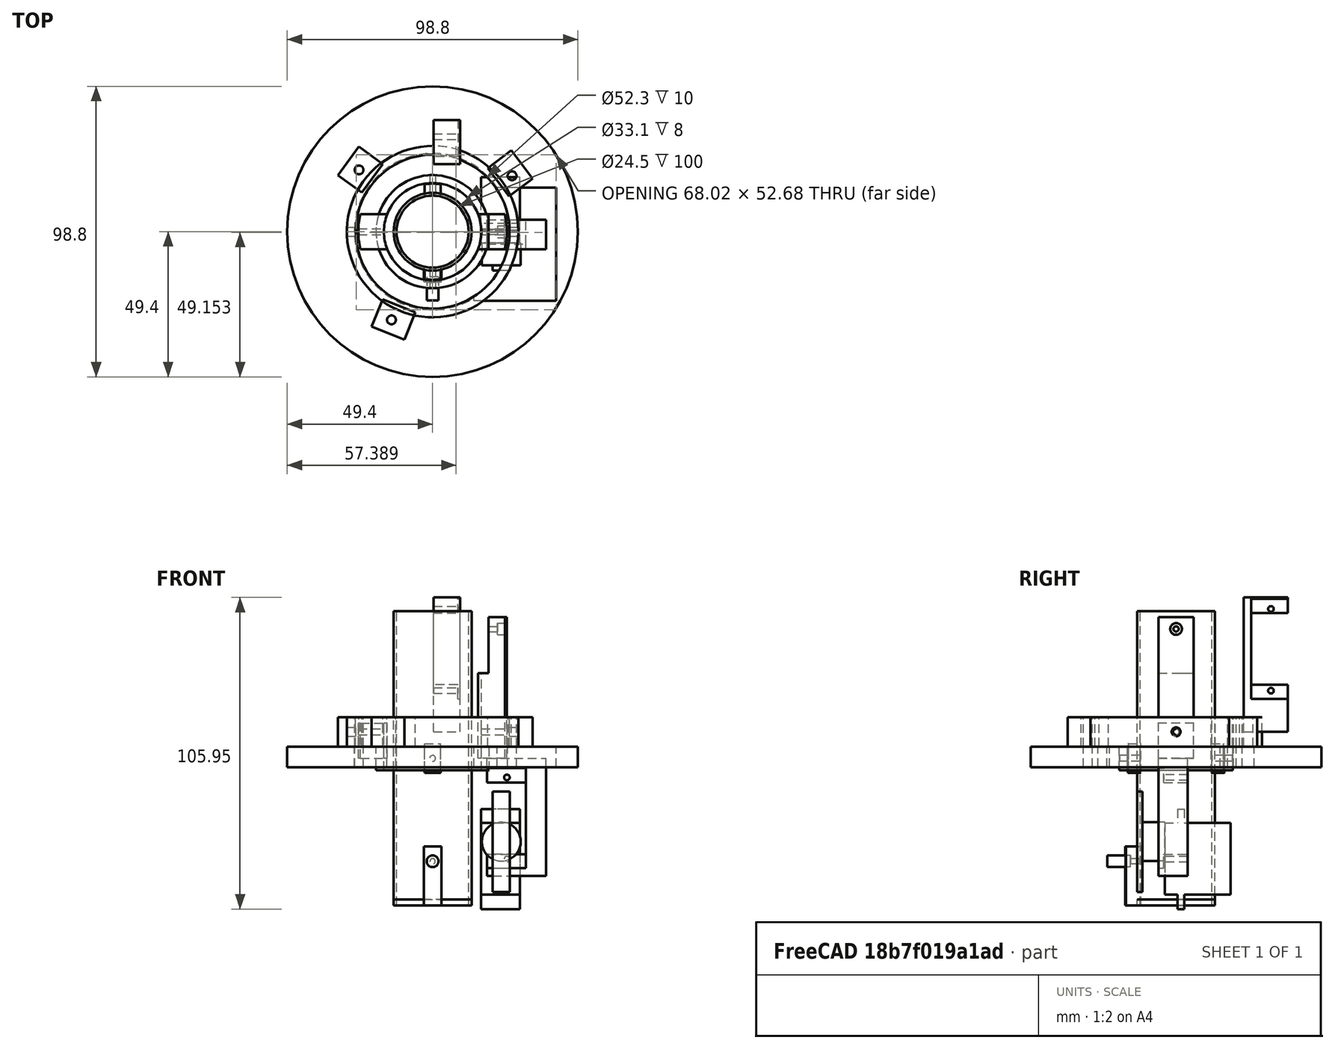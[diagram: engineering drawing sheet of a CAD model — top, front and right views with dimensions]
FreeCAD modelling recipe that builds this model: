
FCSTD DOCUMENT  (FreeCAD 0.18R16146 (Git))
Label: Gimbal
License: All rights reserved
LicenseURL: http://en.wikipedia.org/wiki/All_rights_reserved
objects: Part::Cylinder×28, Part::Cut×24, Part::Box×18, Part::MultiFuse×16, Spreadsheet::Sheet×1
note: 86 computed .brp shape members not serialized (recipe doc carries the construction recipe); baked Part::Feature solids carry a one-line shape summary decoded from their .brp

FEATURE [Part::Cylinder] Cylinder  label="Estes24mm"
  Angle = 360
  AttacherType = Attacher::AttachEngine3D
  Height = 100
  Radius = 12.25
  expr: Height = Spreadsheet.Estes24mmLength
  expr: Radius = Spreadsheet.Estes24mmRadius
FEATURE [Part::Cylinder] Cylinder001  label="EngineHolder"
  Angle = 360
  AttacherType = Attacher::AttachEngine3D
  Height = 100
  Radius = 13.25
  expr: Radius = Spreadsheet.EngineHolderOuterRadius
  expr: Height = Spreadsheet.EngineHolderLength
FEATURE [Spreadsheet::Sheet] Spreadsheet
  cells = A1=EngineHolderLength; B1(EngineHolderLength)=100; A2=EngineHolderOuterRadius; B2(EngineHolderOuterRadius)=13.25; A3=WidthServo; B3(WidthServo)=13.2; A4=xScrewMountThickness; B4(xScrewMountThickness)=3; A5=ScrewMountZ; B5(ScrewMountZ)=10; A6=ScrewMountX; B6(ScrewMountX)=5.5; C6=For width of ScrewBoss On Motor Mount Tube; A7=Bracket1Thickness; B7(BracketThickness1)=3; A8=Bracket1Height; B8(Bracket1Height)=8; A9=Bracket1InnerTolerance; B9(Bracket1InnerTolerance)=0.3; A10=PushpointFromBottom1; B10(PushpointFromBottom1)=0; C10=Bottom of PushPointProtrusion (what holds the linkage stopper); A11=PushpointHeight1; B11(PushpointHeight1)=4; A12=PushpointLenght1; B12(PushpointLength1)=20; A13=PushpointWidth1; B13(PushpointWidth1)=6; A14=Estes24mmRadius; B14(Estes24mmRadius)=12.25; A15=ServoScrewSeparation; B15(ServoScrewSeparation)=27.8; A16=ScrewMountWidthY; B16(ScrewMountWidthY)=12; C16=For Width of ScrewBoss on Bracket1; A17=Bracket2InnerTolerance; B17(Bracket2InnerTolerance)=0.9; C17=radial distance or wiggle room between bracket 1 and 2; A18=Bracket2Thickness; B18(Bracket2Thickness)=3; C18=thickness of outer bracket (bracket 2); A19=ScrewBracket1Thickness; B19(ScrewBracket1Thickkness)=9; C19=thickness of screw bosses to attach bracket 1 and 2; A20=Estes24mmLength; B20(Estes24mmLength)=100; C20=Length of Engine; actually making it longer to completely hollow cylinder; A21=Bracket1Center; B21(Bracket1Center)=50; C21=Distance from Bottom of EngineHolder to First Bracket (z); A22=YScrewHoleZ; B22(YScrewHoleZ)=5; C22=Distance from Bottom of Y ScrewBoss to ScrewCenter; A23=Bracket1LongZ; B23(Bracket1LongZ)=48; C23=Length of Long Part of Bracket1 Arm; A24=ScrewPointOuterGimbal; B24(ScrewPointOuterGimbal)==Spreadsheet.Bracket1Center + Spreadsheet.Bracket1Height / 2 + Spreadsheet.YScrewHoleZ; C24=Distance from Bottom of Mount to Where Outer Gimbal Screws; A25=DisRotPushPoint; B25(DisRotPushPoint)=35; C25=Distance from Screws to Where Servo Pushes (in Z); A26=LinkageStopperZ; B26(LinkageStopperZ)=15; C26=Distance to LinkageStopperScrewIn from Bottom in Z
FEATURE [Part::Cut] Cut  label="A-EngineHolderSubtractedEngine"
  Base = -> Cylinder001
  Tool = -> Cylinder
FEATURE [Part::Box] Box  label="Cube"
  AttacherType = Attacher::AttachEngine3D
  Height = 24.4
  Length = 13.2
  Width = 22.4
  expr: Length = Spreadsheet.WidthServo
FEATURE [Part::Box] Box001  label="Cube001"
  AttacherType = Attacher::AttachEngine3D
  Height = 34
  Length = 13.2
  Placement = pos=(0,4.3,-4.75) rot=(0,0,1;0rad)
  Width = 2.3
  expr: Length = Spreadsheet.WidthServo
FEATURE [Part::Cylinder] Cylinder002  label="Cylinder"
  Angle = 360
  AttacherType = Attacher::AttachEngine3D
  Height = 7.6
  Placement = pos=(6.35,0,6.35) rot=(1,0,0;1.5708rad)
  Radius = 6.6
  expr: Radius = Spreadsheet.WidthServo / 2
FEATURE [Part::Box] Box002  label="Rotor"
  AttacherType = Attacher::AttachEngine3D
  Height = 34.2
  Length = 5.8
  Placement = pos=(3.45,-9.4,-10.75) rot=(0,0,1;0rad)
  Width = 1.8
FEATURE [Part::MultiFuse] Fusion  label="Servo"
  Placement = pos=(29.7,-3.85,28) rot=(0,1,0;3.14159rad)
  Shapes = -> [Box,Cylinder002,Box002,Box001]
  expr: Placement.Base.y = 9.4 - Spreadsheet.EngineHolderOuterRadius
FEATURE [Part::Cylinder] Cylinder004  label="MountBracket1"
  Angle = 360
  AttacherType = Attacher::AttachEngine3D
  Height = 10
  Placement = pos=(0,0,45) rot=(0,0,1;0rad)
  Radius = 16.35
  expr: Placement.Base.z = Spreadsheet.EngineHolderLength / 2 - Spreadsheet.ScrewMountZ / 2
  expr: Radius = Spreadsheet.EngineHolderOuterRadius + Spreadsheet.xScrewMountThickness + Spreadsheet.Bracket1InnerTolerance / 3
  expr: Height = Spreadsheet.ScrewMountZ
FEATURE [Part::Cylinder] Cylinder005  label="Estes24mm001"
  Angle = 360
  AttacherType = Attacher::AttachEngine3D
  Height = 94.5
  Radius = 12.25
  expr: Radius = Spreadsheet.Estes24mmRadius
FEATURE [Part::Cut] Cut001  label="MountBracket"
  Base = -> Cylinder004
  Tool = -> Cylinder005
FEATURE [Part::Box] Box003  label="Cube002"
  AttacherType = Attacher::AttachEngine3D
  Height = 100
  Length = 16.25
  Placement = pos=(2.75,-16.25,0) rot=(0,0,1;0rad)
  Width = 32.5
  expr: Placement.Base.y = -Spreadsheet.EngineHolderOuterRadius - Spreadsheet.xScrewMountThickness
  expr: Width = Spreadsheet.EngineHolderOuterRadius * 2 + Spreadsheet.xScrewMountThickness * 2
  expr: Length = Spreadsheet.EngineHolderOuterRadius + Spreadsheet.xScrewMountThickness
  expr: Height = Spreadsheet.EngineHolderLength
  expr: Placement.Base.x = Spreadsheet.ScrewMountX / 2
FEATURE [Part::Box] Box004  label="Cube003"
  AttacherType = Attacher::AttachEngine3D
  Height = 100
  Length = 16
  Placement = pos=(-18.75,-16.25,0) rot=(0,0,1;0rad)
  Width = 32.5
  expr: Placement.Base.y = -Spreadsheet.EngineHolderOuterRadius - Spreadsheet.xScrewMountThickness
  expr: Width = Spreadsheet.EngineHolderOuterRadius * 2 + Spreadsheet.xScrewMountThickness * 2
  expr: Length = Spreadsheet.EngineHolderOuterRadius + Spreadsheet.ScrewMountX / 2
  expr: Height = Spreadsheet.EngineHolderLength
  expr: Placement.Base.x = -Spreadsheet.ScrewMountX - Spreadsheet.EngineHolderOuterRadius
FEATURE [Part::MultiFuse] Fusion001  label="SubtractionCubesForMountBracket"
  Shapes = -> [Box003,Box004]
FEATURE [Part::Cut] Cut002  label="MountBracketForScrews"
  Base = -> Cut001
  Tool = -> Fusion001
FEATURE [Part::Cylinder] Cylinder006  label="OuterCylinderBracket1"
  Angle = 360
  AttacherType = Attacher::AttachEngine3D
  Height = 8
  Radius = 19.25
  expr: Radius = Spreadsheet.EngineHolderOuterRadius + Spreadsheet.xScrewMountThickness + Spreadsheet.BracketThickness1
  expr: Height = Spreadsheet.Bracket1Height
FEATURE [Part::Cylinder] Cylinder007  label="InnerCylinderBracket"
  Angle = 360
  AttacherType = Attacher::AttachEngine3D
  Height = 8
  Radius = 16.55
  expr: Radius = Spreadsheet.EngineHolderOuterRadius + Spreadsheet.xScrewMountThickness + Spreadsheet.Bracket1InnerTolerance
  expr: Height = Spreadsheet.Bracket1Height
FEATURE [Part::Cut] Cut003  label="Bracket1"
  Base = -> Cylinder006
  Placement = pos=(0,0,46) rot=(0,0,1;0rad)
  Tool = -> Cylinder007
  expr: Placement.Base.z = Spreadsheet.Bracket1Center - Spreadsheet.Bracket1Height / 2
FEATURE [Part::Cylinder] Cylinder008  label="PushPoint1"
  Angle = 360
  AttacherType = Attacher::AttachEngine3D
  Height = 20
  Radius = 17.25
  expr: Height = Spreadsheet.PushpointLength1
  expr: Radius = Spreadsheet.EngineHolderOuterRadius + Spreadsheet.PushpointHeight1
  expr: Placement.Base.z = Spreadsheet.PushpointFromBottom1
FEATURE [Part::Cylinder] Cylinder009  label="Estes24mm002"
  Angle = 360
  AttacherType = Attacher::AttachEngine3D
  Height = 94.5
  Radius = 12.25
  expr: Radius = Spreadsheet.Estes24mmRadius
FEATURE [Part::Cut] Cut004  label="PushpointOne"
  Base = -> Cylinder008
  Tool = -> Cylinder009
FEATURE [Part::Box] Box005  label="Cube004"
  AttacherType = Attacher::AttachEngine3D
  Height = 80
  Length = 50
  Placement = pos=(3,-30,-5) rot=(0,0,1;0rad)
  Width = 100
  expr: Placement.Base.x = Spreadsheet.PushpointWidth1 / 2
FEATURE [Part::Box] Box006  label="Cube005"
  AttacherType = Attacher::AttachEngine3D
  Height = 80
  Length = 60
  Placement = pos=(-63,-30,-5) rot=(0,0,1;0rad)
  Width = 100
  expr: Placement.Base.x = -60 - Spreadsheet.PushpointWidth1 / 2
FEATURE [Part::Box] Box007  label="Cube006"
  AttacherType = Attacher::AttachEngine3D
  Height = 80
  Length = 40
  Placement = pos=(-20,0,-5) rot=(0,0,1;0rad)
  Width = 30
FEATURE [Part::MultiFuse] Fusion002  label="SubtractionCubes"
  Shapes = -> [Box005,Box006,Box007]
FEATURE [Part::Cut] Cut005  label="PushPointFirst"
  Base = -> Cut004
  Tool = -> Fusion002
FEATURE [Part::Cylinder] Cylinder010  label="BigHead"
  Angle = 360
  AttacherType = Attacher::AttachEngine3D
  Height = 7.9
  Placement = pos=(0,-3.1,0) rot=(1,0,0;1.5708rad)
  Radius = 2
FEATURE [Part::Cylinder] Cylinder011  label="SmallScrewCylinder"
  Angle = 360
  AttacherType = Attacher::AttachEngine3D
  Height = 3.1
  Placement = pos=(0,0,0) rot=(1,0,0;1.5708rad)
  Radius = 0.9
FEATURE [Part::MultiFuse] Fusion006  label="LinkageStopper"
  Placement = pos=(0,-12.35,15) rot=(0,0,1;0rad)
  Shapes = -> [Cylinder010,Cylinder011]
  expr: Placement.Base.z = Spreadsheet.LinkageStopperZ
  expr: Placement.Base.y = -(Spreadsheet.EngineHolderOuterRadius + Spreadsheet.PushpointHeight1) + 4.9
  expr: Placement.Base.x = 0
FEATURE [Part::MultiFuse] Fusion007  label="LinkageStopper001"
  Placement = pos=(0,-12.35,15) rot=(0,0,1;0rad)
  Shapes = -> [Cylinder010,Cylinder011]
  expr: Placement.Base.z = Spreadsheet.LinkageStopperZ
  expr: Placement.Base.y = -(Spreadsheet.EngineHolderOuterRadius + Spreadsheet.PushpointHeight1) + 4.9
  expr: Placement.Base.x = 0
FEATURE [Part::Cut] Cut008  label="A-PushPointWithHole"
  Base = -> Cut005
  Tool = -> Fusion007
FEATURE [Part::Cylinder] Cylinder012  label="ScrewSubtractionCylinderForFirstMount"
  Angle = 360
  AttacherType = Attacher::AttachEngine3D
  Height = 90
  Placement = pos=(0,45,50) rot=(1,0,0;1.5708rad)
  Radius = 1
  expr: Placement.Base.z = Spreadsheet.EngineHolderLength / 2
FEATURE [Part::Cut] Cut009  label="A-MountBracketForScrewsWithScrewHole"
  Base = -> Cut002
  Tool = -> Cylinder012
FEATURE [Part::Cylinder] Cylinder013  label="ScrewSubtractionCylinderForFirstMount001"
  Angle = 360
  AttacherType = Attacher::AttachEngine3D
  Height = 90
  Placement = pos=(0,45,50) rot=(1,0,0;1.5708rad)
  Radius = 1
  expr: Placement.Base.z = Spreadsheet.Bracket1Center
FEATURE [Part::Cut] Cut010  label="B-Bracket1WithScrewHole"
  Base = -> Cut003
  Tool = -> Cylinder013
FEATURE [Part::Box] Box012  label="HolderCube001"
  AttacherType = Attacher::AttachEngine3D
  Height = 40
  Length = 20
  Placement = pos=(18.5,-6,10) rot=(0,0,1;0rad)
  Width = 10
FEATURE [Part::MultiFuse] Fusion008  label="Servo001"
  Placement = pos=(18.5,-10.75,17.4) rot=(0,0,1;0rad)
  Shapes = -> [Box,Cylinder002,Box002,Box001]
FEATURE [Part::Cut] Cut011  label="ServoHolder001"
  Base = -> Box012
  Tool = -> Fusion008
FEATURE [Part::Cylinder] Cylinder014  label="ScrewSubtractionCylinderForServo1"
  Angle = 360
  AttacherType = Attacher::AttachEngine3D
  Height = 90
  Placement = pos=(23.25,47,13.5) rot=(1,0,0;1.5708rad)
  Radius = 0.95
FEATURE [Part::Cylinder] Cylinder015  label="ScrewSubtractionCylinderForServo002"
  Angle = 360
  AttacherType = Attacher::AttachEngine3D
  Height = 90
  Placement = pos=(23.25,47,41.3) rot=(1,0,0;1.5708rad)
  Radius = 0.95
  expr: Placement.Base.z = 13.5 + Spreadsheet.ServoScrewSeparation
FEATURE [Part::MultiFuse] Fusion009  label="ServoScrewRemovalCylinders"
  Placement = pos=(2,0,2.2) rot=(0,0,1;0rad)
  Shapes = -> [Cylinder015,Cylinder014]
FEATURE [Part::Cut] Cut012  label="B-ServoHolderWithScrewsRemoved"
  Base = -> Cut011
  Tool = -> Fusion009
FEATURE [Part::Cylinder] Cylinder016  label="OuterCylinderBracket002"
  Angle = 360
  AttacherType = Attacher::AttachEngine3D
  Height = 48
  Radius = 25.25
  expr: Radius = Spreadsheet.EngineHolderOuterRadius + Spreadsheet.xScrewMountThickness + Spreadsheet.ScrewBracket1Thickkness
  expr: Height = Spreadsheet.Bracket1LongZ
FEATURE [Part::Cylinder] Cylinder017  label="InnerCylinderBracket001"
  Angle = 360
  AttacherType = Attacher::AttachEngine3D
  Height = 48
  Radius = 16.55
  expr: Radius = Spreadsheet.EngineHolderOuterRadius + Spreadsheet.xScrewMountThickness + Spreadsheet.Bracket1InnerTolerance
  expr: Height = Spreadsheet.Bracket1LongZ
FEATURE [Part::Cut] Cut013  label="Bracket1toBracket2"
  Base = -> Cylinder016
  Placement = pos=(0,0,50) rot=(0,0,1;0rad)
  Tool = -> Cylinder017
  expr: Placement.Base.z = Spreadsheet.EngineHolderLength / 2 + 0 * Spreadsheet.Bracket1Height / 2
FEATURE [Part::Cylinder] Cylinder018  label="ScrewSubtractionCylinderForSecondMount"
  Angle = 360
  AttacherType = Attacher::AttachEngine3D
  Height = 90
  Placement = pos=(-45,0,59) rot=(0,1,0;1.5708rad)
  Radius = 1
  expr: Placement.Base.z = Spreadsheet.Bracket1Center + Spreadsheet.Bracket1Height / 2 + Spreadsheet.YScrewHoleZ
FEATURE [Part::Cut] Cut014  label="Bracket1toBracket2Connection"
  Base = -> Cut013
  Tool = -> Cylinder018
FEATURE [Part::Box] Box013  label="Cube007"
  AttacherType = Attacher::AttachEngine3D
  Height = 150
  Length = 100
  Placement = pos=(-50,6,0) rot=(0,0,1;0rad)
  Width = 100
  expr: Placement.Base.y = Spreadsheet.ScrewMountWidthY / 2
FEATURE [Part::Box] Box014  label="Cube008"
  AttacherType = Attacher::AttachEngine3D
  Height = 150
  Length = 100
  Placement = pos=(-50,-6,0) rot=(0,0,-1;1.5708rad)
  Width = 100
  expr: Placement.Base.y = -Spreadsheet.ScrewMountWidthY / 2
FEATURE [Part::MultiFuse] Fusion010  label="SubtractionCubesForYBracket"
  Shapes = -> [Box013,Box014]
FEATURE [Part::Cut] Cut015  label="InnerYScrewBoss"
  Base = -> Cut014
  Tool = -> Fusion010
FEATURE [Part::Cylinder] Cylinder019  label="Bracket1Outer"
  Angle = 360
  AttacherType = Attacher::AttachEngine3D
  Height = 10
  Radius = 29.15
  expr: Radius = Spreadsheet.EngineHolderOuterRadius + Spreadsheet.xScrewMountThickness + Spreadsheet.BracketThickness1 + Spreadsheet.Bracket2InnerTolerance + Spreadsheet.ScrewBracket1Thickkness
FEATURE [Part::Cylinder] Cylinder020  label="Bracket1Inner"
  Angle = 360
  AttacherType = Attacher::AttachEngine3D
  Height = 10
  Radius = 26.15
  expr: Radius = Spreadsheet.EngineHolderOuterRadius + Spreadsheet.xScrewMountThickness + Spreadsheet.ScrewBracket1Thickkness + Spreadsheet.Bracket2InnerTolerance
FEATURE [Part::Cut] Cut016  label="Bracket2Solid"
  Base = -> Cylinder019
  Placement = pos=(0,0,54) rot=(0,0,1;0rad)
  Tool = -> Cylinder020
  expr: Placement.Base.z = Spreadsheet.EngineHolderLength / 2 + Spreadsheet.Bracket1Height / 2
FEATURE [Part::Cylinder] Cylinder021  label="ScrewSubtractionCylinderForSecondMount001"
  Angle = 360
  AttacherType = Attacher::AttachEngine3D
  Height = 90
  Placement = pos=(-45,0,59) rot=(0,1,0;1.5708rad)
  Radius = 1.5
  expr: Placement.Base.z = Spreadsheet.Bracket1Center + Spreadsheet.Bracket1Height / 2 + Spreadsheet.YScrewHoleZ
FEATURE [Part::Cut] Cut017  label="C-Bracket2WithScrewHoles"
  Base = -> Cut016
  Tool = -> Cylinder021
FEATURE [Part::Box] Box015  label="SubtractionCubeBackLongBracket"
  AttacherType = Attacher::AttachEngine3D
  Height = 100
  Length = 50
  Placement = pos=(-50,-50,62) rot=(0,0,1;0rad)
  Width = 100
  expr: Placement.Base.z = Spreadsheet.EngineHolderLength / 2 + Spreadsheet.Bracket1Height + Spreadsheet.Bracket1Height / 2
FEATURE [Part::Cut] Cut018  label="YScrewBossPlus2ndPushLength"
  Base = -> Cut015
  Tool = -> Box015
FEATURE [Part::Cylinder] Cylinder022  label="PushPointOuterGimbal"
  Angle = 360
  AttacherType = Attacher::AttachEngine3D
  Height = 90
  Placement = pos=(-45,0,94) rot=(0,1,0;1.5708rad)
  Radius = 0.1
  expr: Placement.Base.z = Spreadsheet.DisRotPushPoint + Spreadsheet.ScrewPointOuterGimbal
FEATURE [Part::MultiFuse] Fusion012  label="ServoScrewRemovalCylinders001"
  Placement = pos=(0,0,0.5) rot=(0,0,1;0rad)
  Shapes = -> [Cylinder015,Cylinder014]
FEATURE [Part::MultiFuse] Fusion013  label="Servo002"
  Placement = pos=(16.5,-3.85,16) rot=(0,0,1;0rad)
  Shapes = -> [Box,Cylinder002,Box002,Box001]
  expr: Placement.Base.y = 9.4 - Spreadsheet.EngineHolderOuterRadius
FEATURE [Part::MultiFuse] Fusion014  label="Servo2wSubtractionHoles"
  Placement = pos=(11.3,9,59) rot=(0,0,1;1.5708rad)
  Shapes = -> [Fusion013,Fusion012]
FEATURE [Part::Cut] Cut019  label="YScrewBossPlusPushArm"
  Base = -> Cut018
  Tool = -> Cylinder022
FEATURE [Part::Box] Box016  label="Servo2Block"
  AttacherType = Attacher::AttachEngine3D
  Height = 45.7
  Length = 9
  Placement = pos=(0.3,23,59) rot=(0,0,1;0rad)
  Width = 15
FEATURE [Part::Cut] Cut020  label="C-Servo2Holder"
  Base = -> Box016
  Tool = -> Fusion014
FEATURE [Part::Box] Box017  label="SubtractionBlockPushArm"
  AttacherType = Attacher::AttachEngine3D
  Height = 21
  Length = 10
  Placement = pos=(9,-8,79) rot=(0,0,1;0rad)
  Width = 16
FEATURE [Part::Cut] Cut021  label="YScrewBossesPlusPushArm"
  Base = -> Cut019
  Tool = -> Box017
FEATURE [Part::MultiFuse] Fusion015  label="LinkageStopper002"
  Placement = pos=(19,0,94) rot=(0,0,1;1.5708rad)
  Shapes = -> [Cylinder010,Cylinder011]
  expr: Placement.Base.z = Spreadsheet.DisRotPushPoint + Spreadsheet.ScrewPointOuterGimbal
  expr: Placement.Base.y = 0
FEATURE [Part::Cut] Cut022  label="B-YScrewBossPlusPushArmSubtractLinkageStopper"
  Base = -> Cut021
  Tool = -> Fusion015
FEATURE [Part::Cylinder] Cylinder023  label="FourInchOuterTube"
  Angle = 360
  AttacherType = Attacher::AttachEngine3D
  Height = 7
  Radius = 49.4
FEATURE [Part::Cylinder] Cylinder024  label="FourInchInner"
  Angle = 360
  AttacherType = Attacher::AttachEngine3D
  Height = 7
  Radius = 26.6
FEATURE [Part::Cut] Cut023  label="FourInchTube"
  Base = -> Cylinder023
  Placement = pos=(0,0,47) rot=(0,0,1;0rad)
  Tool = -> Cylinder024
FEATURE [Part::Box] Box018  label="ScrewBoxBlock1"
  AttacherType = Attacher::AttachEngine3D
  Height = 10
  Length = 10
  Placement = pos=(26,12,54) rot=(0,0,1;0.645772rad)
  Width = 12
  expr: Placement.Base.z = Spreadsheet.EngineHolderLength / 2 + Spreadsheet.Bracket1Height / 2
FEATURE [Part::Box] Box019  label="ScrewBoxBlock002"
  AttacherType = Attacher::AttachEngine3D
  Height = 10
  Length = 10
  Placement = pos=(-17,23,54) rot=(0,0,1;2.51327rad)
  Width = 12
  expr: Placement.Base.z = Spreadsheet.EngineHolderLength / 2 + Spreadsheet.Bracket1Height / 2
FEATURE [Part::Box] Box020  label="ScrewBoxBlock003"
  AttacherType = Attacher::AttachEngine3D
  Height = 10
  Length = 10
  Placement = pos=(-17,-23,54) rot=(0,0,-1;1.95477rad)
  Width = 12
  expr: Placement.Base.z = Spreadsheet.EngineHolderLength / 2 + Spreadsheet.Bracket1Height / 2
FEATURE [Part::Cylinder] Cylinder025  label="MountScrew1"
  Angle = 360
  AttacherType = Attacher::AttachEngine3D
  Height = 100
  Placement = pos=(27,19,0) rot=(0,0,1;0rad)
  Radius = 1.5
FEATURE [Part::Cylinder] Cylinder026  label="MountScrew002"
  Angle = 360
  AttacherType = Attacher::AttachEngine3D
  Height = 100
  Placement = pos=(-25,21,0) rot=(0,0,1;0rad)
  Radius = 1.5
FEATURE [Part::Cylinder] Cylinder027  label="MountScrew003"
  Angle = 360
  AttacherType = Attacher::AttachEngine3D
  Height = 100
  Placement = pos=(-14,-30,0) rot=(0,0,1;0rad)
  Radius = 1.5
FEATURE [Part::MultiFuse] Fusion016  label="MountScrews"
  Shapes = -> [Cylinder025,Cylinder027,Cylinder026]
FEATURE [Part::MultiFuse] Fusion017  label="MountBlocks"
  Shapes = -> [Box018,Box019,Box020]
FEATURE [Part::Cut] Cut024  label="C-MountBlocksWithScrewHoles"
  Base = -> Fusion017
  Tool = -> Fusion016
FEATURE [Part::Box] Box021  label="ServoCutoutWMargin"
  AttacherType = Attacher::AttachEngine3D
  Height = 100
  Length = 28
  Placement = pos=(14,-23.5,0) rot=(0,0,1;0rad)
  Width = 38.5
FEATURE [Part::MultiFuse] Fusion018  label="MountScrews001"
  Shapes = -> [Cylinder025,Cylinder027,Cylinder026]
FEATURE [Part::MultiFuse] Fusion019  label="ServoCutoutAndScrewHoles"
  Shapes = -> [Fusion018,Box021]
FEATURE [Part::Cut] Cut025  label="D-TubeHolder"
  Base = -> Cut023
  Tool = -> Fusion019
FEATURE [Part::Cylinder] Cylinder029  label="A-CapEnd"
  Angle = 360
  AttacherType = Attacher::AttachEngine3D
  Height = 2
  Radius = 13.25
  expr: Radius = Spreadsheet.EngineHolderOuterRadius
